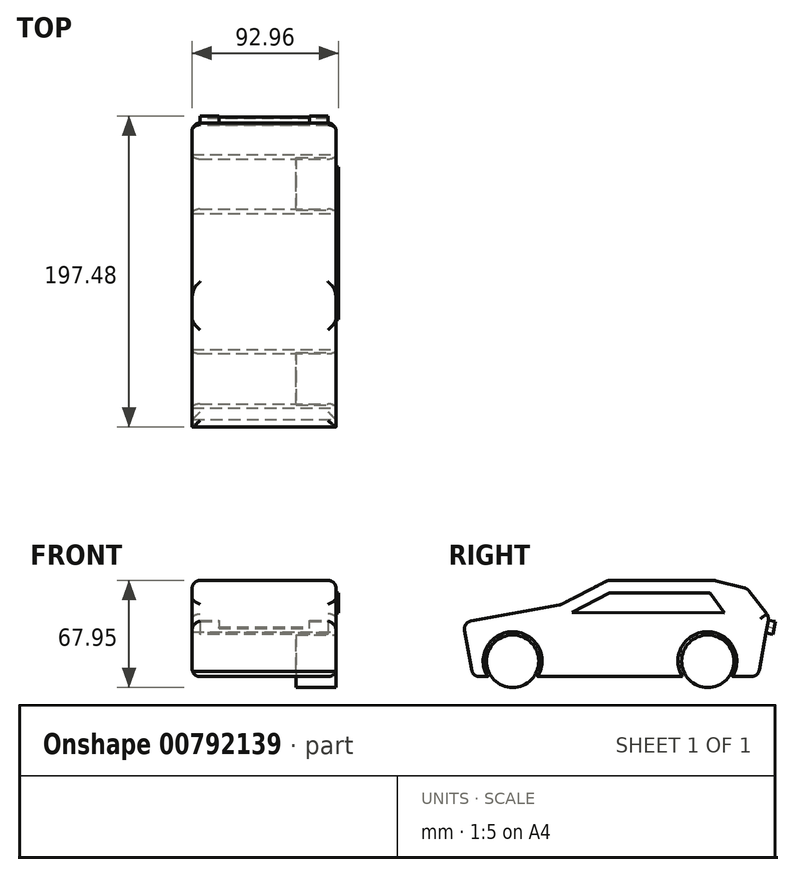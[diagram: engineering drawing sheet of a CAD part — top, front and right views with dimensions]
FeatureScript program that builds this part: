
annotation { "Feature Type Name" : "Feature", "Feature Type Description" : "" }
export const myFeature = defineFeature(function(context is Context, id is Id, definition is map)
    precondition{}
    {
        {
            var Q0;
            Q0=qCreatedBy(makeId("Right.planeOp"),FACE);
            var sketch = newSketch(context, id + "F0", { "sketchPlane" : qUnion([Q0])});
            skLineSegment(sketch, "E0.bottom", {"start": v(-99.78, 40.14) * mm, "end": v(99.38, 40.14) * mm});
            skLineSegment(sketch, "E0.top", {"start": v(-99.78, -55.87) * mm, "end": v(99.38, -55.87) * mm});
            skLineSegment(sketch, "E0.left", {"start": v(-99.78, 40.14) * mm, "end": v(-99.78, -55.87) * mm});
            skLineSegment(sketch, "E0.right", {"start": v(99.38, 40.14) * mm, "end": v(99.38, -55.87) * mm});
            skSolve(sketch);
        }
        {
            var Q0;
            Q0=makeQuery(id+"F0.imprint","IMPRINT",FACE,{"disambiguationData":[TD([[makeQuery(id+"F0.imprint","IMPRINT",EDGE,{"derivedFrom":sQuery(id+"F0.wireOp",EDGE,"E0.bottom")}),-1.0]])]});
            extrude(context, id + "F1", {"entities" : qUnion([Q0]), "depth" : 45.72 * mm, "offsetDistance" : 25.4 * mm, "hasSecondDirection" : true, "secondDirectionOppositeDirection" : true, "secondDirectionDepth" : 45.72 * mm});
        }
        {
            var Q0;
            Q0=makeQuery(id+"F1.opExtrude","CAP_FACE",FACE,{"disambiguationData":[OSD([sQuery(id+"F0.wireOp",EDGE,"E0.bottom"),sQuery(id+"F0.wireOp",EDGE,"E0.top"),sQuery(id+"F0.wireOp",EDGE,"E0.left"),sQuery(id+"F0.wireOp",EDGE,"E0.right")])],"isStart":false});
            var sketch = newSketch(context, id + "F2", { "sketchPlane" : qUnion([Q0])});
            skLineSegment(sketch, "E1", {"start": v(-99.78, -55.87) * mm, "end": v(-94.16, -52.44) * mm});
            skLineSegment(sketch, "E2", {"start": v(-94.16, -52.44) * mm, "end": v(-99.78, -21.5) * mm});
            skLineSegment(sketch, "E3", {"start": v(-99.78, -21.5) * mm, "end": v(-37.96, -10.26) * mm});
            skLineSegment(sketch, "E4", {"start": v(-37.96, -10.26) * mm, "end": v(-7.93, 5.22) * mm});
            skLineSegment(sketch, "E5", {"start": v(-7.93, 5.22) * mm, "end": v(60.04, 5.22) * mm});
            skLineSegment(sketch, "E6", {"start": v(60.04, 5.22) * mm, "end": v(80.67, 0) * mm});
            skLineSegment(sketch, "E7", {"start": v(80.67, 0) * mm, "end": v(94.43, -17.79) * mm});
            skLineSegment(sketch, "E8", {"start": v(94.43, -17.79) * mm, "end": v(87.55, -55.87) * mm});
            skLineSegment(sketch, "E9", {"start": v(87.55, -55.87) * mm, "end": v(99.38, -55.87) * mm});
            skLineSegment(sketch, "E10", {"start": v(99.38, -55.87) * mm, "end": v(99.38, 40.14) * mm});
            skLineSegment(sketch, "E11", {"start": v(99.38, 40.14) * mm, "end": v(-99.78, 40.14) * mm});
            skLineSegment(sketch, "E12", {"start": v(-99.78, 40.14) * mm, "end": v(-99.78, -55.87) * mm});
            skSolve(sketch);
        }
        {
            var Q0;
            Q0 = qSketchRegion(id + "F2", true);
            extrude(context, id + "F3", {"entities" : qUnion([Q0]), "operationType" : NewBodyOperationType.REMOVE, "oppositeDirection" : true, "depth" : 175.26 * mm, "offsetDistance" : 25.4 * mm});
        }
        {
            var Q0;
            Q0=makeQuery(id+"F3.boolean.opBoolean","COPY",FACE,{"derivedFrom":makeQuery(id+"F3.opExtrude","SWEPT_FACE",FACE,{"disambiguationData":[OSD([sQuery(id+"F2.wireOp",EDGE,"E3")])]})});
            fillet(context, id + "F4", {"entities" : qUnion([Q0]), "radius" : 5.08 * mm, "tangentPropagation" : true, "allowEdgeOverflow" : false});
        }
        {
            var Q0;
            Q0=makeQuery(id+"F3.boolean.opBoolean","COPY",FACE,{"derivedFrom":makeQuery(id+"F3.opExtrude","SWEPT_FACE",FACE,{"disambiguationData":[OSD([sQuery(id+"F2.wireOp",EDGE,"E5")])]})});
            var Q1;
            Q1=makeQuery(id+"F3.boolean.opBoolean","COPY",FACE,{"derivedFrom":makeQuery(id+"F3.opExtrude","SWEPT_FACE",FACE,{"disambiguationData":[OSD([sQuery(id+"F2.wireOp",EDGE,"E6")])]})});
            var Q2;
            Q2=makeQuery(id+"F3.boolean.opBoolean","COPY",FACE,{"derivedFrom":makeQuery(id+"F3.opExtrude","SWEPT_FACE",FACE,{"disambiguationData":[OSD([sQuery(id+"F2.wireOp",EDGE,"E7")])]})});
            fillet(context, id + "F5", {"entities" : qUnion([Q0, Q1, Q2]), "radius" : 5.08 * mm, "tangentPropagation" : true, "allowEdgeOverflow" : false});
        }
        {
            var Q0;
            Q0=makeQuery(id+"F3.boolean.opBoolean","COPY",FACE,{"derivedFrom":makeQuery(id+"F3.opExtrude","SWEPT_FACE",FACE,{"disambiguationData":[OSD([sQuery(id+"F2.wireOp",EDGE,"E8")])]})});
            fillet(context, id + "F6", {"entities" : qUnion([Q0]), "radius" : 5.08 * mm, "tangentPropagation" : true, "allowEdgeOverflow" : false});
        }
        {
            var Q0;
            Q0=makeQuery(id+"F1.opExtrude","SWEPT_FACE",FACE,{"disambiguationData":[OSD([sQuery(id+"F0.wireOp",EDGE,"E0.top")])]});
            fillet(context, id + "F7", {"entities" : qUnion([Q0]), "radius" : 5.08 * mm, "tangentPropagation" : true, "allowEdgeOverflow" : false});
        }
        {
            var Q0;
            Q0=makeQuery(id+"F1.opExtrude","CAP_FACE",FACE,{"disambiguationData":[OSD([sQuery(id+"F0.wireOp",EDGE,"E0.bottom"),sQuery(id+"F0.wireOp",EDGE,"E0.top"),sQuery(id+"F0.wireOp",EDGE,"E0.left"),sQuery(id+"F0.wireOp",EDGE,"E0.right")])],"isStart":false});
            var sketch = newSketch(context, id + "F8", { "sketchPlane" : qUnion([Q0])});
            skCircle(sketch, "E13", {"center": v(-68.34, -46.09) * mm, "radius": 18.7 * mm});
            skPoint(sketch, "E13.centerSnap0", {"position": v(-68.34, -20.94) * mm});
            skCircle(sketch, "E14.1.0.0", {"center": v(55.36, -46.09) * mm, "radius": 18.7 * mm});
            skSolve(sketch);
        }
        {
            var Q0;
            {var subQ0=sQuery(id+"F8.wireOp",EDGE,"E13");var subQ1=sQuery(id+"F0.wireOp",EDGE,"E0.top");var subQ2=makeQuery(id+"F7.opFillet","BLEND_EDGE",EDGE,{"blendedFrom":[makeQuery(id+"F1.opExtrude","CAP_EDGE",EDGE,{"disambiguationData":[OSD([subQ1])],"isStart":false}),makeQuery(id+"F1.opExtrude","CAP_FACE",FACE,{"disambiguationData":[OSD([sQuery(id+"F0.wireOp",EDGE,"E0.bottom"),subQ1,sQuery(id+"F0.wireOp",EDGE,"E0.left"),sQuery(id+"F0.wireOp",EDGE,"E0.right")])],"isStart":false})],"blendedInto":[makeQuery(id+"F1.opExtrude","CAP_FACE",FACE,{"disambiguationData":[OSD([sQuery(id+"F0.wireOp",EDGE,"E0.bottom"),subQ1,sQuery(id+"F0.wireOp",EDGE,"E0.left"),sQuery(id+"F0.wireOp",EDGE,"E0.right")])],"isStart":false})]});var subQ3=makeQuery(id+"F8.imprint","INTERSECT",VERTEX,{"disambiguationData":[OD(0.0)],"derivedFrom":[subQ2,subQ0]});Q0=makeQuery(id+"F8.imprint","IMPRINT",FACE,{"disambiguationData":[TD([[makeQuery(id+"F8.imprint","IMPRINT",EDGE,{"disambiguationData":[TD([[subQ3,1.0]])],"derivedFrom":subQ0}),1.0]])]});}
            var Q1;
            {var subQ0=sQuery(id+"F8.wireOp",EDGE,"E13");var subQ1=sQuery(id+"F0.wireOp",EDGE,"E0.top");var subQ2=makeQuery(id+"F7.opFillet","BLEND_EDGE",EDGE,{"blendedFrom":[makeQuery(id+"F1.opExtrude","CAP_EDGE",EDGE,{"disambiguationData":[OSD([subQ1])],"isStart":false}),makeQuery(id+"F1.opExtrude","CAP_FACE",FACE,{"disambiguationData":[OSD([sQuery(id+"F0.wireOp",EDGE,"E0.bottom"),subQ1,sQuery(id+"F0.wireOp",EDGE,"E0.left"),sQuery(id+"F0.wireOp",EDGE,"E0.right")])],"isStart":false})],"blendedInto":[makeQuery(id+"F1.opExtrude","CAP_FACE",FACE,{"disambiguationData":[OSD([sQuery(id+"F0.wireOp",EDGE,"E0.bottom"),subQ1,sQuery(id+"F0.wireOp",EDGE,"E0.left"),sQuery(id+"F0.wireOp",EDGE,"E0.right")])],"isStart":false})]});var subQ3=makeQuery(id+"F8.imprint","INTERSECT",VERTEX,{"disambiguationData":[OD(0.0)],"derivedFrom":[subQ2,subQ0]});Q1=makeQuery(id+"F8.imprint","IMPRINT",FACE,{"disambiguationData":[TD([[makeQuery(id+"F8.imprint","IMPRINT",EDGE,{"disambiguationData":[TD([[subQ3,-1.0]])],"derivedFrom":subQ0}),1.0]])]});}
            var Q2;
            {var subQ0=sQuery(id+"F8.wireOp",EDGE,"E14.1.0.0");var subQ1=sQuery(id+"F0.wireOp",EDGE,"E0.top");var subQ2=makeQuery(id+"F7.opFillet","BLEND_EDGE",EDGE,{"blendedFrom":[makeQuery(id+"F1.opExtrude","CAP_EDGE",EDGE,{"disambiguationData":[OSD([subQ1])],"isStart":false}),makeQuery(id+"F1.opExtrude","CAP_FACE",FACE,{"disambiguationData":[OSD([sQuery(id+"F0.wireOp",EDGE,"E0.bottom"),subQ1,sQuery(id+"F0.wireOp",EDGE,"E0.left"),sQuery(id+"F0.wireOp",EDGE,"E0.right")])],"isStart":false})],"blendedInto":[makeQuery(id+"F1.opExtrude","CAP_FACE",FACE,{"disambiguationData":[OSD([sQuery(id+"F0.wireOp",EDGE,"E0.bottom"),subQ1,sQuery(id+"F0.wireOp",EDGE,"E0.left"),sQuery(id+"F0.wireOp",EDGE,"E0.right")])],"isStart":false})]});var subQ3=makeQuery(id+"F8.imprint","INTERSECT",VERTEX,{"disambiguationData":[OD(0.0)],"derivedFrom":[subQ2,subQ0]});Q2=makeQuery(id+"F8.imprint","IMPRINT",FACE,{"disambiguationData":[TD([[makeQuery(id+"F8.imprint","IMPRINT",EDGE,{"disambiguationData":[TD([[subQ3,-1.0]])],"derivedFrom":subQ0}),1.0]])]});}
            var Q3;
            {var subQ0=sQuery(id+"F8.wireOp",EDGE,"E14.1.0.0");var subQ1=sQuery(id+"F0.wireOp",EDGE,"E0.top");var subQ2=makeQuery(id+"F7.opFillet","BLEND_EDGE",EDGE,{"blendedFrom":[makeQuery(id+"F1.opExtrude","CAP_EDGE",EDGE,{"disambiguationData":[OSD([subQ1])],"isStart":false}),makeQuery(id+"F1.opExtrude","CAP_FACE",FACE,{"disambiguationData":[OSD([sQuery(id+"F0.wireOp",EDGE,"E0.bottom"),subQ1,sQuery(id+"F0.wireOp",EDGE,"E0.left"),sQuery(id+"F0.wireOp",EDGE,"E0.right")])],"isStart":false})],"blendedInto":[makeQuery(id+"F1.opExtrude","CAP_FACE",FACE,{"disambiguationData":[OSD([sQuery(id+"F0.wireOp",EDGE,"E0.bottom"),subQ1,sQuery(id+"F0.wireOp",EDGE,"E0.left"),sQuery(id+"F0.wireOp",EDGE,"E0.right")])],"isStart":false})]});var subQ3=makeQuery(id+"F8.imprint","INTERSECT",VERTEX,{"disambiguationData":[OD(0.0)],"derivedFrom":[subQ2,subQ0]});Q3=makeQuery(id+"F8.imprint","IMPRINT",FACE,{"disambiguationData":[TD([[makeQuery(id+"F8.imprint","IMPRINT",EDGE,{"disambiguationData":[TD([[subQ3,1.0]])],"derivedFrom":subQ0}),1.0]])]});}
            extrude(context, id + "F9", {"entities" : qUnion([Q0, Q1, Q2, Q3]), "operationType" : NewBodyOperationType.REMOVE, "oppositeDirection" : true, "depth" : 212.6 * mm, "offsetDistance" : 25.4 * mm});
        }
        {
            var Q0;
            Q0=makeQuery(id+"F1.opExtrude","CAP_FACE",FACE,{"disambiguationData":[OSD([sQuery(id+"F0.wireOp",EDGE,"E0.bottom"),sQuery(id+"F0.wireOp",EDGE,"E0.top"),sQuery(id+"F0.wireOp",EDGE,"E0.left"),sQuery(id+"F0.wireOp",EDGE,"E0.right")])],"isStart":false});
            var sketch = newSketch(context, id + "F10", { "sketchPlane" : qUnion([Q0])});
            skCircle(sketch, "E15", {"center": v(-68.34, -46.09) * mm, "radius": 16.64 * mm});
            skCircle(sketch, "E16.1.0.0", {"center": v(55.61, -46.09) * mm, "radius": 16.64 * mm});
            skSolve(sketch);
        }
        {
            var Q0;
            Q0=makeQuery(id+"F10.imprint","IMPRINT",FACE,{"disambiguationData":[TD([[makeQuery(id+"F10.imprint","IMPRINT",EDGE,{"derivedFrom":sQuery(id+"F10.wireOp",EDGE,"E16.1.0.0")}),1.0]])]});
            var Q1;
            Q1=makeQuery(id+"F10.imprint","IMPRINT",FACE,{"disambiguationData":[TD([[makeQuery(id+"F10.imprint","IMPRINT",EDGE,{"derivedFrom":sQuery(id+"F10.wireOp",EDGE,"E15")}),1.0]])]});
            extrude(context, id + "F11", {"entities" : qUnion([Q0, Q1]), "operationType" : NewBodyOperationType.ADD, "oppositeDirection" : true, "depth" : 25.4 * mm, "offsetDistance" : 25.4 * mm});
        }
        {
            var Q0;
            Q0=makeQuery(id+"F3.boolean.opBoolean","COPY",FACE,{"derivedFrom":makeQuery(id+"F3.opExtrude","SWEPT_FACE",FACE,{"disambiguationData":[OSD([sQuery(id+"F2.wireOp",EDGE,"E8")])]})});
            var sketch = newSketch(context, id + "F12", { "sketchPlane" : qUnion([Q0])});
            skLineSegment(sketch, "E17", {"start": v(-40.64, -2.99) * mm, "end": v(-40.64, -11.2) * mm});
            skLineSegment(sketch, "E18", {"start": v(-40.64, -11.2) * mm, "end": v(40.64, -11.2) * mm});
            skLineSegment(sketch, "E19", {"start": v(40.64, -11.2) * mm, "end": v(40.64, -2.99) * mm});
            skLineSegment(sketch, "E20", {"start": v(40.64, -2.99) * mm, "end": v(28.76, -2.99) * mm});
            skLineSegment(sketch, "E21", {"start": v(28.76, -2.99) * mm, "end": v(28.76, -7.45) * mm});
            skLineSegment(sketch, "E22", {"start": v(28.76, -7.45) * mm, "end": v(-28.9, -7.45) * mm});
            skLineSegment(sketch, "E23", {"start": v(-28.9, -7.45) * mm, "end": v(-28.9, -2.99) * mm});
            skLineSegment(sketch, "E24", {"start": v(-28.9, -2.99) * mm, "end": v(-40.64, -2.99) * mm});
            skSolve(sketch);
        }
        {
            var Q0;
            Q0 = qSketchRegion(id + "F12", true);
            extrude(context, id + "F13", {"entities" : qUnion([Q0]), "operationType" : NewBodyOperationType.ADD, "depth" : 4.57 * mm, "offsetDistance" : 25.4 * mm});
        }
        {
            var Q0;
            Q0=makeQuery(id+"F1.opExtrude","CAP_FACE",FACE,{"disambiguationData":[OSD([sQuery(id+"F0.wireOp",EDGE,"E0.bottom"),sQuery(id+"F0.wireOp",EDGE,"E0.top"),sQuery(id+"F0.wireOp",EDGE,"E0.left"),sQuery(id+"F0.wireOp",EDGE,"E0.right")])],"isStart":false});
            var sketch = newSketch(context, id + "F14", { "sketchPlane" : qUnion([Q0])});
            skLineSegment(sketch, "E25", {"start": v(-30.7, -15.02) * mm, "end": v(-6.7, -2.64) * mm});
            skPoint(sketch, "E25.startSnap0", {"position": v(-36.35, -15.02) * mm});
            skLineSegment(sketch, "E26", {"start": v(-6.7, -2.64) * mm, "end": v(56.85, -2.64) * mm});
            skLineSegment(sketch, "E27", {"start": v(56.85, -2.64) * mm, "end": v(66.1, -15.4) * mm});
            skLineSegment(sketch, "E28", {"start": v(66.1, -15.4) * mm, "end": v(-30.7, -15.02) * mm});
            skSolve(sketch);
        }
        {
            var Q0;
            Q0 = qSketchRegion(id + "F14", true);
            extrude(context, id + "F15", {"entities" : qUnion([Q0]), "operationType" : NewBodyOperationType.ADD, "depth" : 1.52 * mm, "offsetDistance" : 25.4 * mm});
        }
    });
